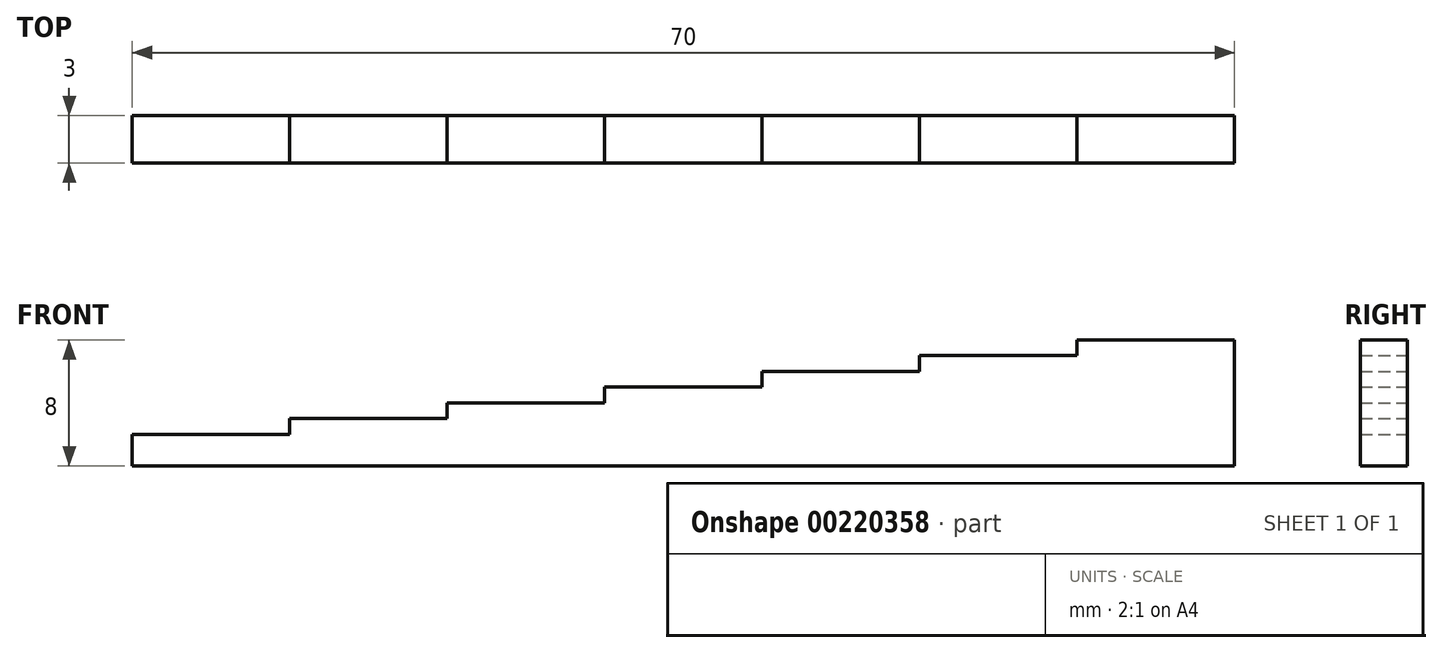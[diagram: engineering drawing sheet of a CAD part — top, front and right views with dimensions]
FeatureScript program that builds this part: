
annotation { "Feature Type Name" : "Feature", "Feature Type Description" : "" }
export const myFeature = defineFeature(function(context is Context, id is Id, definition is map)
    precondition{}
    {
        {
            var Q0;
            Q0=qCreatedBy(makeId("Front.planeOp"),FACE);
            var sketch = newSketch(context, id + "F0", { "sketchPlane" : qUnion([Q0])});
            skLineSegment(sketch, "E0", {"start": v(-40, 0) * mm, "end": v(30, 0) * mm});
            skLineSegment(sketch, "E1", {"start": v(-40, 2) * mm, "end": v(-40, 0) * mm});
            skLineSegment(sketch, "E2", {"start": v(-40, 2) * mm, "end": v(-30, 2) * mm});
            skLineSegment(sketch, "E3", {"start": v(-30, 2) * mm, "end": v(-30, 3) * mm});
            skLineSegment(sketch, "E4", {"start": v(-30, 3) * mm, "end": v(-20, 3) * mm});
            skLineSegment(sketch, "E5", {"start": v(-20, 3) * mm, "end": v(-20, 4) * mm});
            skLineSegment(sketch, "E6", {"start": v(-20, 4) * mm, "end": v(-10, 4) * mm});
            skLineSegment(sketch, "E7", {"start": v(-10, 4) * mm, "end": v(-10, 5) * mm});
            skLineSegment(sketch, "E8", {"start": v(-10, 5) * mm, "end": v(0, 5) * mm});
            skLineSegment(sketch, "E9", {"start": v(0, 5) * mm, "end": v(0, 6) * mm});
            skLineSegment(sketch, "E10", {"start": v(0, 6) * mm, "end": v(10, 6) * mm});
            skLineSegment(sketch, "E11", {"start": v(10, 6) * mm, "end": v(10, 7) * mm});
            skLineSegment(sketch, "E12", {"start": v(10, 7) * mm, "end": v(20, 7) * mm});
            skLineSegment(sketch, "E13", {"start": v(20, 8) * mm, "end": v(20, 7) * mm});
            skLineSegment(sketch, "E14", {"start": v(20, 8) * mm, "end": v(30, 8) * mm});
            skLineSegment(sketch, "E15", {"start": v(30, 8) * mm, "end": v(30, 0) * mm});
            skSolve(sketch);
        }
        {
            var Q0;
            Q0=makeQuery(id+"F0.imprint","IMPRINT",FACE,{"disambiguationData":[TD([[makeQuery(id+"F0.imprint","IMPRINT",EDGE,{"derivedFrom":sQuery(id+"F0.wireOp",EDGE,"E0")}),1.0]])]});
            extrude(context, id + "F1", {"entities" : qUnion([Q0]), "depth" : 3 * mm});
        }
    });
